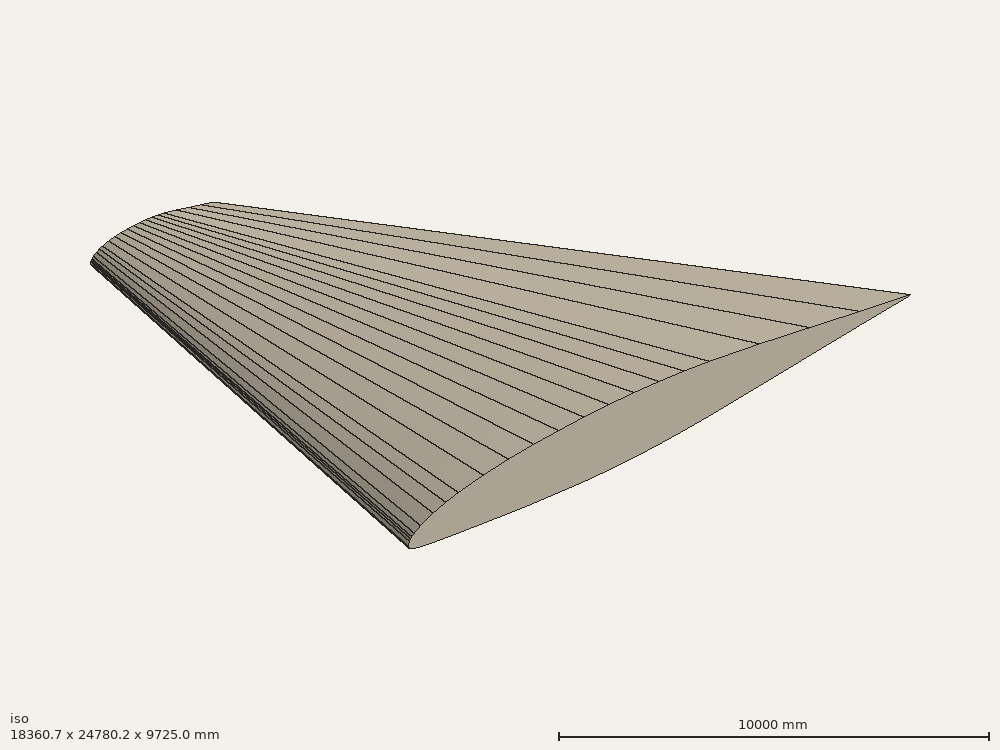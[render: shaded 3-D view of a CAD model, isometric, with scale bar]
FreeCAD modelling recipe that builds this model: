
FCSTD DOCUMENT  (FreeCAD 0.19R)
Label: b737_base-c_cleanup
License: All rights reserved
LicenseURL: http://en.wikipedia.org/wiki/All_rights_reserved
objects: Sketcher::SketchObject×3, Part::FeaturePython×2, App::DocumentObjectGroup×1, Part::Feature×1, Spreadsheet::Sheet×1
note: 6 computed .brp shape members not serialized (recipe doc carries the construction recipe); baked Part::Feature solids carry a one-line shape summary decoded from their .brp

FEATURE [App::DocumentObjectGroup] b737d
FEATURE [Part::Feature] Wire
  Placement = pos=(0,0,0) rot=(1,0,0;1.5708rad)
  shape: bbox 1 x 2e-07 x 0.1082 mm, 0 faces, 0 solids (baked)
FEATURE [Part::FeaturePython] Clone  label="WireScaled"  # Draft clone (typed FeaturePython)
  AttacherType = Attacher::AttachEngine3D
  Fuse = false
  Objects = -> [Wire]
  Placement = pos=(0,0,0) rot=(1,0,0;1.5708rad)
  Scale = (16550.6,16550.6,16550.6)
  expr: .Scale.z = Spreadsheet.cr
  expr: .Scale.y = Spreadsheet.cr
  expr: .Scale.x = Spreadsheet.cr
FEATURE [Sketcher::SketchObject] Sketch  label="SketchThicknessMax"
  ExternalGeometry = -> [Clone]
  Placement = pos=(0,0,0) rot=(1,0,0;1.5708rad)
  sketch-geometry (1):
    g0: LineSegment StartX=5792.71 StartY=1122.13 StartZ=0 EndX=5792.71 EndY=-642.163 EndZ=0
  constraints (3):
    c: DistanceY(g-4,g-3) = 1764.29  'thkmax'
    c: Coincident(g0,g-3)
    c: Coincident(g0,g-4)
FEATURE [Sketcher::SketchObject] Sketch001
  ExternalGeometry = -> [Clone]
  Placement = pos=(0,0,0) rot=(0.57735,0.57735,0.57735;2.0944rad)
  expr: Constraints[5] = <<SketchThicknessMax>>.Constraints.thkmax * Spreadsheet.thktaper
  expr: Constraints[4] = Spreadsheet.span / 2
  expr: Constraints[7] = 90 - Spreadsheet.da
  sketch-geometry (3):
    g0: LineSegment StartX=2.492e-13 StartY=1122.13 StartZ=0 EndX=24780.2 EndY=-7897.14 EndZ=0
    g1: LineSegment StartX=0 StartY=-642.163 StartZ=0 EndX=24780.2 EndY=-8602.86 EndZ=0
    g2: LineSegment StartX=24780.2 StartY=-7897.14 StartZ=0 EndX=24780.2 EndY=-8602.86 EndZ=0
  constraints (8):
    c: Coincident(g0,g-3)
    c: Coincident(g1,g-4)
    c: Coincident(g2,g0)
    c: Coincident(g2,g1)
    c: DistanceX(g-1,g1) = 24780.2
    c: DistanceY(g2,g2) = 705.718
    c: Vertical(g2)
    c: Angle(g-2,g0) = 1.22173
FEATURE [Sketcher::SketchObject] Sketch002
  ExternalGeometry = -> [Clone]
  expr: Constraints[6] = Spreadsheet.sa
  expr: Constraints[5] = Spreadsheet.span / 2
  expr: Constraints[7] = Spreadsheet.ct
  sketch-geometry (3):
    g0: LineSegment StartX=16550.6 StartY=0 StartZ=0 EndX=18360.7 EndY=24780.2 EndZ=0
    g1: LineSegment StartX=0 StartY=0 StartZ=0 EndX=14306.9 EndY=24780.2 EndZ=0
    g2: LineSegment StartX=14306.9 StartY=24780.2 StartZ=0 EndX=18360.7 EndY=24780.2 EndZ=0
  constraints (8):
    c: Coincident(g0,g-3)
    c: Coincident(g1,g-1)
    c: Coincident(g2,g1)
    c: Coincident(g2,g0)
    c: Horizontal(g2)
    c: DistanceY(g1,g0) = 24780.2
    c: Angle(g-1,g1) = 1.0472
    c: DistanceX(g2,g2) = 4053.84
FEATURE [Spreadsheet::Sheet] Spreadsheet
  cells = A1=Boeing 747; A2=Span; B2(span)=49560.5; A4=Center chord (c0); B4(cr)=16550.6; A5=Tip chord (ct); B5(ct)=4053.84; A8=Thickness taper ratio; B8(thktaper)=0.4; A9=Sweep angle; B9(sa)=60; A10=Dihedral angle; B10(da)=20; A11=Rib count; B11(rc)=8
FEATURE [Part::FeaturePython] CurvedArray  # WARN: FeaturePython — macro-defined, semantics opaque (R4)
  Axis = (0,1,0)
  Base = -> Clone
  Distribution = 0
  DistributionReverse = false
  Hullcurves = -> [Sketch001,Sketch002]
  Items = 8
  OffsetEnd = 0
  OffsetStart = 0
  Solid = true
  Surface = false
  Twist = 0
  expr: Items = Spreadsheet.rc
